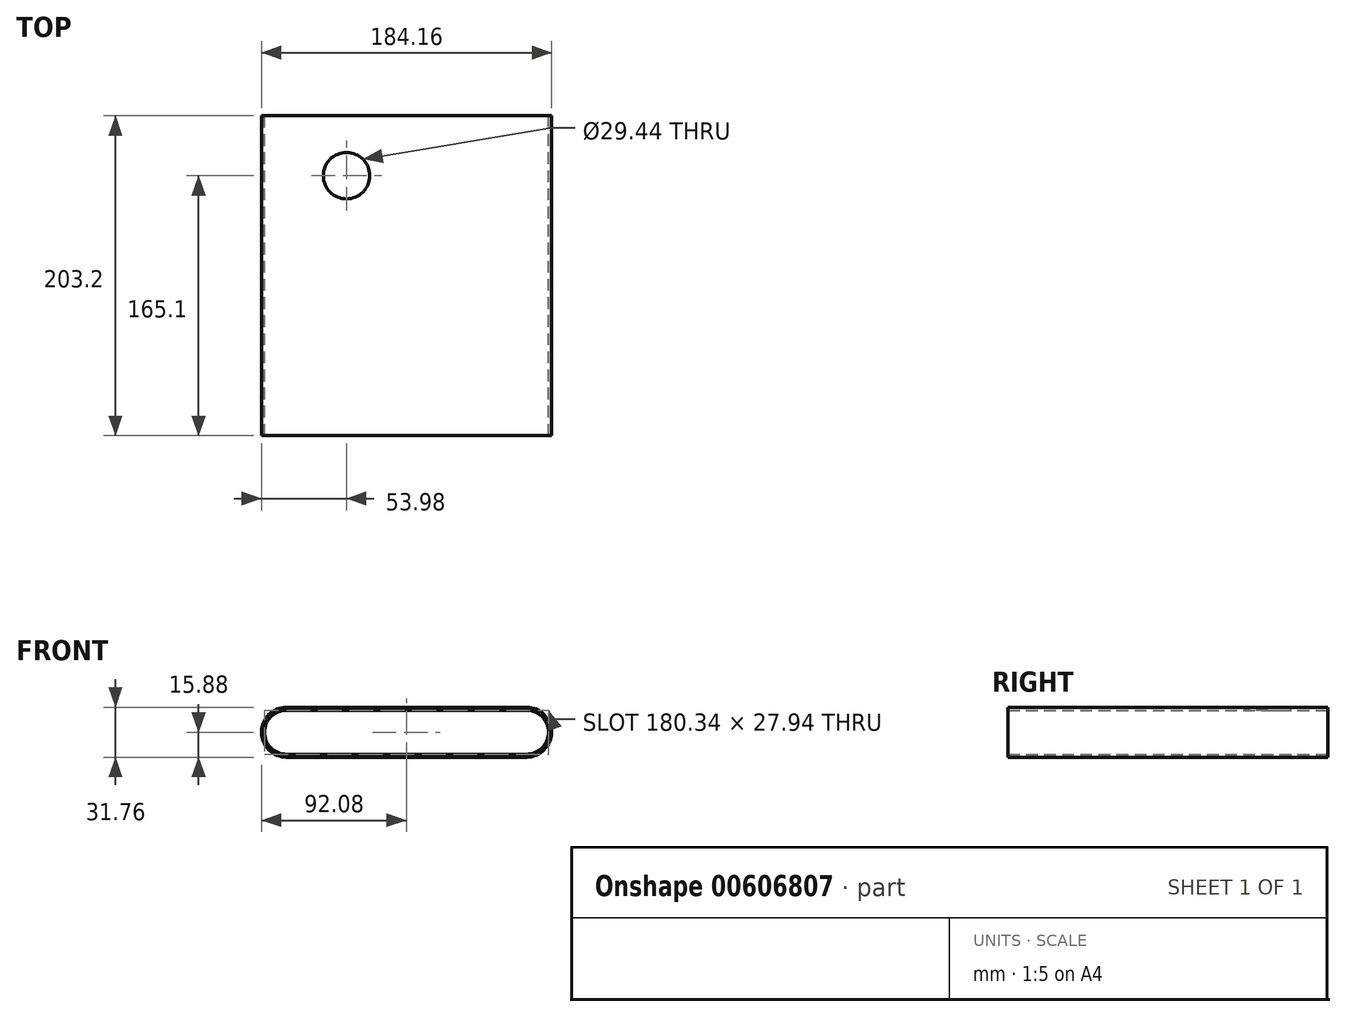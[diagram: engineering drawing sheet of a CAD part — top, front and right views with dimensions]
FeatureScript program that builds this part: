
annotation { "Feature Type Name" : "Feature", "Feature Type Description" : "" }
export const myFeature = defineFeature(function(context is Context, id is Id, definition is map)
    precondition{}
    {
        {
            var Q0;
            Q0=qCreatedBy(makeId("Front.planeOp"),FACE);
            var sketch = newSketch(context, id + "F0", { "sketchPlane" : qUnion([Q0])});
            skLineSegment(sketch, "E0", {"start": v(-76.2, 0) * mm, "end": v(76.2, 0) * mm});
            skLineSegment(sketch, "E1.bottom", {"start": v(76.2, -15.87) * mm, "end": v(-76.2, -15.88) * mm});
            skLineSegment(sketch, "E1.top", {"start": v(76.2, 15.88) * mm, "end": v(-76.2, 15.87) * mm});
            skLineSegment(sketch, "E1.left", {"start": v(76.2, -15.87) * mm, "end": v(76.2, 15.88) * mm});
            skLineSegment(sketch, "E1.right", {"start": v(-76.2, -15.88) * mm, "end": v(-76.2, 15.87) * mm});
            skPoint(sketch, "E1.middle", {"position": v(0, 0) * mm});
            skCircle(sketch, "E2", {"center": v(-76.2, 0) * mm, "radius": 15.88 * mm});
            skCircle(sketch, "E3", {"center": v(76.2, 0) * mm, "radius": 15.88 * mm});
            skSolve(sketch);
        }
        {
            var Q0;
            Q0=qCreatedBy(makeId("Front.planeOp"),FACE);
            var sketch = newSketch(context, id + "F1", { "sketchPlane" : qUnion([Q0])});
            skLineSegment(sketch, "E4.bottom", {"start": v(76.2, 13.97) * mm, "end": v(-76.2, 13.97) * mm});
            skLineSegment(sketch, "E4.top", {"start": v(76.2, -13.97) * mm, "end": v(-76.2, -13.97) * mm});
            skLineSegment(sketch, "E4.left", {"start": v(76.2, 13.97) * mm, "end": v(76.2, -13.97) * mm});
            skLineSegment(sketch, "E4.right", {"start": v(-76.2, 13.97) * mm, "end": v(-76.2, -13.97) * mm});
            skPoint(sketch, "E4.middle", {"position": v(0, 0) * mm});
            skCircle(sketch, "E5", {"center": v(-76.2, 0) * mm, "radius": 13.97 * mm});
            skCircle(sketch, "E6", {"center": v(76.2, 0) * mm, "radius": 13.97 * mm});
            skSolve(sketch);
        }
        {
            var Q0;
            Q0 = qSketchRegion(id + "F0", true);
            extrude(context, id + "F2", {"entities" : qUnion([Q0]), "depth" : 203.2 * mm, "offsetDistance" : 25.4 * mm});
        }
        {
            var Q0;
            Q0 = qSketchRegion(id + "F1", true);
            extrude(context, id + "F3", {"entities" : qUnion([Q0]), "operationType" : NewBodyOperationType.REMOVE, "endBound" : BoundingType.THROUGH_ALL, "depth" : 25.4 * mm, "offsetDistance" : 25.4 * mm});
        }
        {
            var Q0;
            Q0=makeQuery(id+"F2.opExtrude","SWEPT_FACE",FACE,{"disambiguationData":[OSD([sQuery(id+"F0.wireOp",EDGE,"E1.top")])]});
            var sketch = newSketch(context, id + "F4", { "sketchPlane" : qUnion([Q0])});
            skCircle(sketch, "E7", {"center": v(-38.1, -38.1) * mm, "radius": 14.72 * mm});
            skSolve(sketch);
        }
        {
            var Q0;
            Q0 = qSketchRegion(id + "F4", true);
            extrude(context, id + "F5", {"entities" : qUnion([Q0]), "operationType" : NewBodyOperationType.REMOVE, "oppositeDirection" : true, "depth" : 12.7 * mm, "offsetDistance" : 25.4 * mm});
        }
    });
